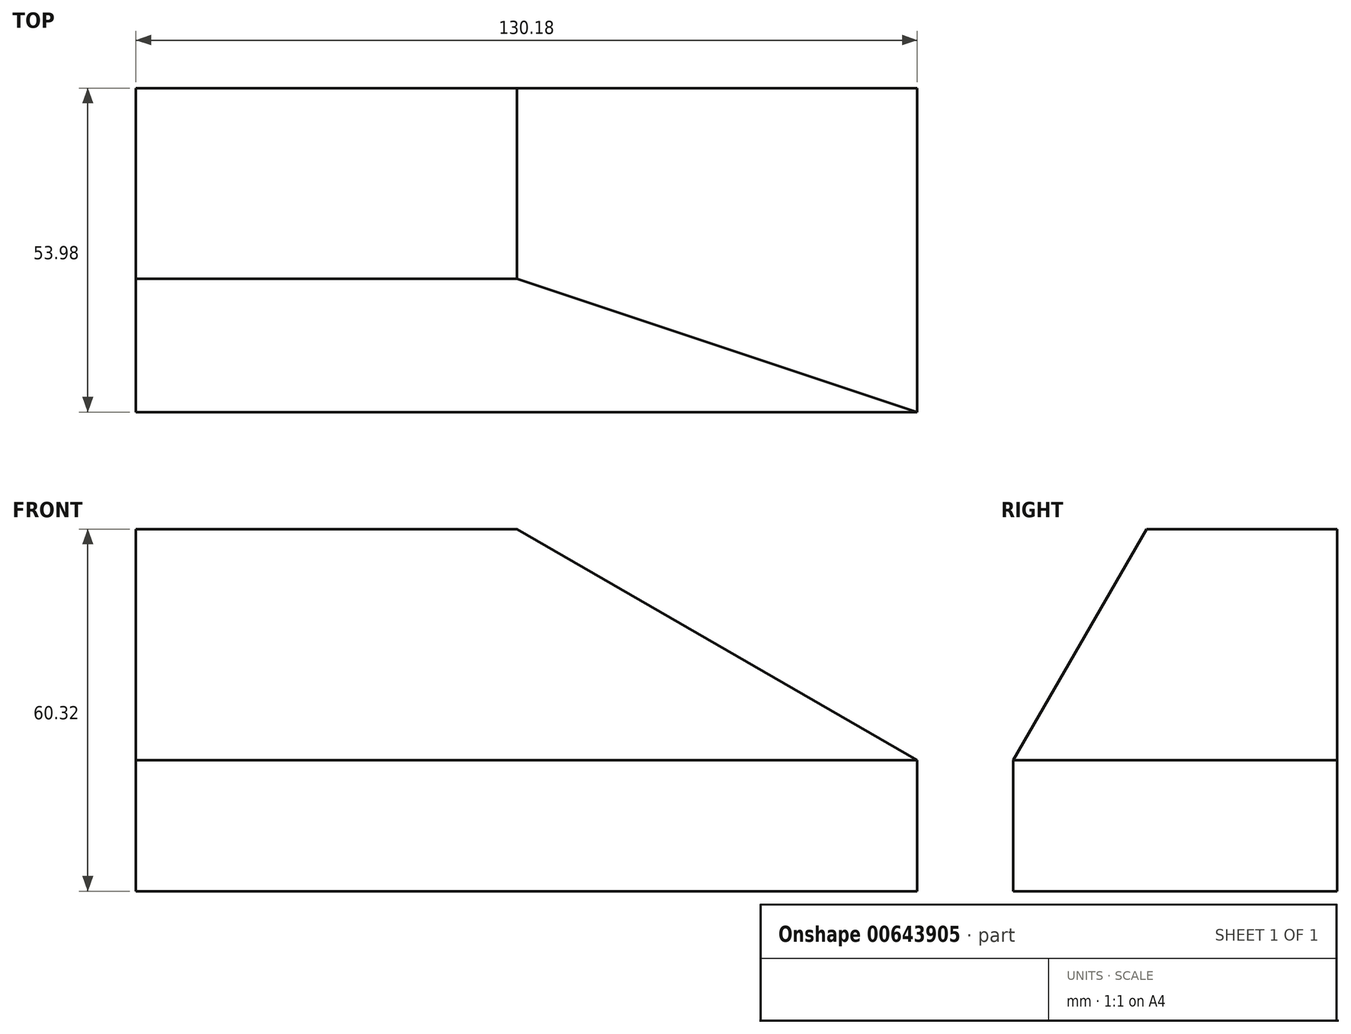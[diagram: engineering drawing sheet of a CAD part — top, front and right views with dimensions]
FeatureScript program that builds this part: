
annotation { "Feature Type Name" : "Feature", "Feature Type Description" : "" }
export const myFeature = defineFeature(function(context is Context, id is Id, definition is map)
    precondition{}
    {
        {
            var Q0;
            Q0=qCreatedBy(makeId("Front.planeOp"),FACE);
            var sketch = newSketch(context, id + "F0", { "sketchPlane" : qUnion([Q0])});
            skLineSegment(sketch, "E0.top", {"start": v(-65.09, -30.16) * mm, "end": v(65.09, -30.16) * mm});
            skLineSegment(sketch, "E0.left", {"start": v(-65.09, 30.16) * mm, "end": v(-65.09, -30.16) * mm});
            skPoint(sketch, "E0.middle", {"position": v(0, 0) * mm});
            skLineSegment(sketch, "E1", {"start": v(-1.59, 30.16) * mm, "end": v(65.09, -8.33) * mm});
            skLineSegment(sketch, "E2", {"start": v(-65.09, 30.16) * mm, "end": v(-1.59, 30.16) * mm});
            skLineSegment(sketch, "E3", {"start": v(65.09, -8.33) * mm, "end": v(65.09, -30.16) * mm});
            skLineSegment(sketch, "E4", {"start": v(-65.09, -30.16) * mm, "end": v(-65.09, 30.16) * mm});
            skLineSegment(sketch, "E5", {"start": v(-1.59, 30.16) * mm, "end": v(65.09, 30.16) * mm});
            skLineSegment(sketch, "E6", {"start": v(65.09, 30.16) * mm, "end": v(65.09, -8.33) * mm});
            skSolve(sketch);
        }
        {
            var Q0;
            Q0=makeQuery(id+"F0.imprint","IMPRINT",FACE,{"disambiguationData":[TD([[makeQuery(id+"F0.imprint","IMPRINT",EDGE,{"derivedFrom":sQuery(id+"F0.wireOp",EDGE,"E0.top")}),1.0]])]});
            extrude(context, id + "F1", {"entities" : qUnion([Q0]), "depth" : 53.97 * mm, "offsetDistance" : 25.4 * mm});
        }
        {
            var Q0;
            Q0=qCreatedBy(makeId("Right.planeOp"),FACE);
            var sketch = newSketch(context, id + "F2", { "sketchPlane" : qUnion([Q0])});
            skLineSegment(sketch, "E7", {"start": v(-53.98, 30.16) * mm, "end": v(-53.98, -8.33) * mm});
            skLineSegment(sketch, "E8", {"start": v(-53.98, -8.33) * mm, "end": v(-31.75, 30.16) * mm});
            skLineSegment(sketch, "E9", {"start": v(-53.98, 30.16) * mm, "end": v(-31.75, 30.16) * mm});
            skSolve(sketch);
        }
        {
            var Q0;
            Q0=makeQuery(id+"F2.imprint","IMPRINT",FACE,{"disambiguationData":[TD([[makeQuery(id+"F2.imprint","IMPRINT",EDGE,{"derivedFrom":sQuery(id+"F2.wireOp",EDGE,"E7")}),1.0]])]});
            extrude(context, id + "F3", {"entities" : qUnion([Q0]), "operationType" : NewBodyOperationType.REMOVE, "endBound" : BoundingType.SYMMETRIC, "oppositeDirection" : true, "depth" : 130.17 * mm, "offsetDistance" : 25.4 * mm});
        }
    });
